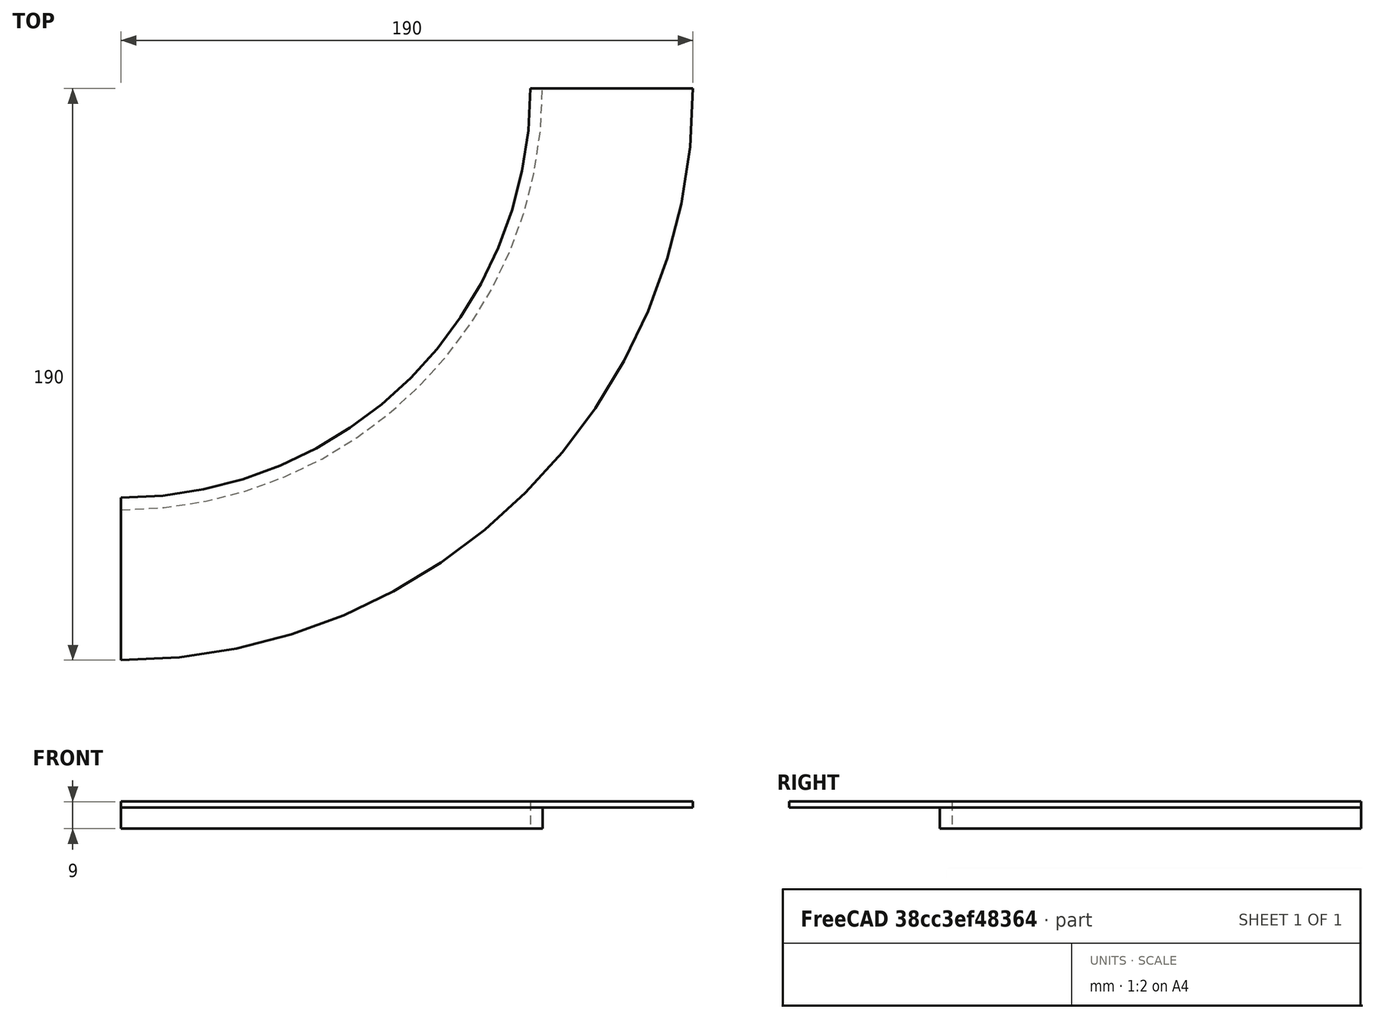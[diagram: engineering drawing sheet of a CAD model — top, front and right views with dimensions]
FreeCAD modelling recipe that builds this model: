
FCSTD DOCUMENT  (FreeCAD 1.1R39748 (Git))
Label: Кружок
License: All rights reserved
LicenseURL: https://en.wikipedia.org/wiki/All_rights_reserved
objects: App::Point×1, Sketcher::SketchObject×1, PartDesign::Revolution×1, PartDesign::Body×1, Measure::MeasureDistance×1, App::DocumentObjectGroup×1
note: 6 computed .brp shape members not serialized (recipe doc carries the construction recipe); baked Part::Feature solids carry a one-line shape summary decoded from their .brp

FEATURE [App::Point] Origin001
  Role = Origin
FEATURE [Sketcher::SketchObject] Sketch
  ArcFitTolerance = 1e-06
  AttachmentSupport = -> [XZ_Plane]
  ExternalTypes = [0]
  FullyConstrained = false
  MakeInternals = false
  MapMode = 5
  Placement = pos=(0,0,0) rot=(1,0,0;1.5708rad)
  sketch-geometry (8):
    g0: LineSegment [constr] StartX=-140 StartY=25.0209 StartZ=0 EndX=140 EndY=25.0209 EndZ=0
    g1: LineSegment StartX=140 StartY=25.0209 StartZ=0 EndX=136 EndY=25.0209 EndZ=0
    g2: LineSegment StartX=136 StartY=25.0209 StartZ=0 EndX=136 EndY=16.0209 EndZ=0
    g3: LineSegment StartX=136 StartY=16.0209 StartZ=0 EndX=140 EndY=16.0209 EndZ=0
    g4: LineSegment StartX=140 StartY=16.0209 StartZ=0 EndX=140 EndY=23.0209 EndZ=0
    g5: LineSegment StartX=140 StartY=23.0209 StartZ=0 EndX=190 EndY=23.0209 EndZ=0
    g6: LineSegment StartX=190 StartY=23.0209 StartZ=0 EndX=190 EndY=25.0209 EndZ=0
    g7: LineSegment StartX=190 StartY=25.0209 StartZ=0 EndX=140 EndY=25.0209 EndZ=0
  constraints (22):
    c: Symmetric(g0,g0,g-2)
    c: DistanceX(g0,g0) = 280
    c: Coincident(g0,g1)
    c: Coincident(g1,g2)
    c: Vertical(g2)
    c: Coincident(g2,g3)
    c: Coincident(g3,g4)
    c: Vertical(g4)
    c: Coincident(g4,g5)
    c: Horizontal(g5)
    c: Coincident(g5,g6)
    c: Coincident(g6,g7)
    c: Coincident(g7,g1)
    c: Horizontal(g7)
    c: PointOnObject(g1,g0)
    c: Vertical(g6)
    c: DistanceX(g3,g3) = 4
    c: Horizontal(g3)
    c: DistanceY(g4,g4) = 7
    c: Vertical(g4,g0)
    c: DistanceY(g6,g6) = 2
    c: DistanceX(g7,g7) = 50
FEATURE [PartDesign::Revolution] Revolution
  Angle = 90
  Angle2 = 60
  Axis = (0,2e-16,1)
  Base = (0,0,0)
  Placement = pos=(0,0,0) rot=(1,0,0;1.5708rad)
  Profile = -> Sketch
  ReferenceAxis = -> Sketch [V_Axis]
  Refine = true
  Reversed = true
  Suppressed = false
  Type = 0
FEATURE [PartDesign::Body] Body  label="Тело"
  AllowCompound = false
  Group = -> [Sketch,Revolution]
  Origin = -> Origin
  Tip = -> Revolution
FEATURE [Measure::MeasureDistance] Distance  label="Distance: 268,70 mm"
  Distance = 268.701
  DistanceX = 190
  DistanceY = 190
  DistanceZ = 4.26e-14
  Element1 = -> Body [Revolution.Vertex10]
  Element2 = -> Body [Revolution.Vertex9]
  Position1 = (2.11e-14,-190,23.0209)
  Position2 = (190,5.1e-15,23.0209)
FEATURE [App::DocumentObjectGroup] Measurements
  Group = -> [Distance]
